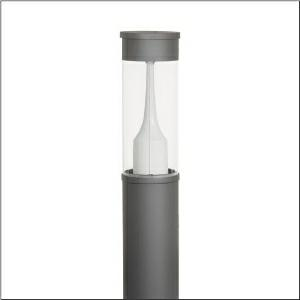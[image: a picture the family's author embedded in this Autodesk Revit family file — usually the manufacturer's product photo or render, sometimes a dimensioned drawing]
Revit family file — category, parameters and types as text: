
# Revit family: city-light_400_iq___st1_2a_5xa5305kf14h_7e7c
name_source: partatom
category: Lighting Fixtures
units: mm (PartAtom-declared; Revit-internal decimal feet)

## family parameters
Cut with Voids When Loaded = No
Host = Face
Light Source = No
Part Type = Normal
Room Calculation Point = No
Round Connector Dimension = Use Diameter
Shared = No

## types (1)
- --- (1 x LED, 1540 lm, 10 W, 4000K)
    Apparent Load = 10 VA
    CIE Flux Codes = 22 61 93 96 100
    Color Rendering = 70
    Color Temperature = 4000K
    Default Elevation = 1800 mm
    Description = City-Light 400 iQ, light pillar, Module 540 iQ-SR, primary light control with 3 zone facetted reflector, of plastic, silver coated, highly specular, structured, primary optical cover: cover, of PMMA, transparent, partly coated, light distribution: ST1.2a, primary light characteristic: asymmetric, LED, High Power LED, rated luminous flux: 1.540lm, luminous efficacy: 154lm/W, light colour: 740, colour temperature: 4000K, control gear: iQ Street-Remote, control: pre-setting: logarithmic dimming characteristic, Street-Remote, Auto-Match, Temp-Guard, Lumen-Switch, Night-Set, Smart-Wire, Light-Fading, Desk-Remote (wireless, voltage-free reading and setting of iQ features in the workshop via application-optimized NFC function/RFID function), optimised constant luminous flux control (CLO 2.0), with terminal, 6-pole, max. 2.5mm², mains connection: 230..240V, AC, 50/60Hz, start of lifetime: 10W, end of service life: 10W, reduction: 5W, luminaire housing, cylindrical, of extruded aluminium section, coated, Siteco® metallic grey (DB 702S), length: 4.694mm, diameter: 200mm, Module 540 iQ-SR, traffic white (RAL 9016), equipment: standard, protection rating (complete): IP65, insulation class (complete): insulation class II (safety insulation), certification: CE, ENEC, VDE, packaging unit: 1 piece

Light Distribution: ST1.2a
    Height = 500 mm
    Lamp = 1 x LED
    Lamp Light Flux = 1540 lm
    Lamp Power = 10 W
    Lamp count = 1
    Length = 200 mm  [stored 0.656168 ft]
    Luminous efficacy = 154 lm/W
    Manufacturer = Siteco
    ModVariant = No
    Model = 5XA5305KF14H
    Mounting Place = Floor
    Mounting Type = Freestanding
    Number of Poles = 1
    OnlyDefault = Yes
    Power Factor = 1
    Product Name = City-Light 400 iQ | ST1.2a
    Product group = light pillar
    ProductGroupID = 1301
    Protection Class = Protection class II
    Protection Degree = IP 65
    RLX_Detail_Level = 1
    RLX_Emergency_Light_Flux = 0 lm
    RLX_Emergency_Type = 0
    RLX_Emergency_Type_DB = No
    RlxData = <blob elided: 87377 chars, md5=77d0fdd8>
    Socket = socket
    Standby Power = 0 W
    System Light Flux = 1540 lm
    System Power = 10 W
    Type Comments = factory setting: luminous flux: 100 % | dim-lin: 254 | 401 mA
    Type Image = l_1006914.jpg
    URL = http://relux.com
    VarID = @adj_180539
    Voltage = 0 V
    Weight = 0.00 kg
    Width = 0 mm  [stored 0 ft]

note: [stored X ft] marks values corroborated as IEEE doubles in the binary element streams (Revit-internal decimal feet)

## geometry (parser evidence)
native form markers: Blend x4, Sweep x10
no freeform markers — native parametric forms only
